# Revit family: Deckel mit Drehriegel_für Kabelrinne und Kabelleiter_NB50
name_source: partatom
category: Generic Models
revit_build: Autodesk Revit 2015 (Build: 20140606_1530(x64)
units: mm (PartAtom-declared; Revit-internal decimal feet)

## types (3) — shared parameters
Height = 13 mm
Length = 3000 mm  [stored 9.84252 ft]
Length 1 = 200 mm  [stored 0.656168 ft]
Length 2 = 1500 mm  [stored 4.92126 ft]
Manufacturer = OBO Bettermann
URL = http://www.obo-bettermann.com
Width = 52 mm
Width 1 = 1 mm  [stored 0.00328084 ft]
Width 2 = 27 mm  [stored 0.0885827 ft]

## per-type parameters (varying)
| type | Article Type | GTIN | Manufacturer Art.No. | Material |
| DRL 050 FS | DRL 050 FS

DRL 050 FS
DRL 050 FS | 4012196057856 | 6052053 | Strip galvanised |
| DRL 050 DD | DRL 050 DD | 4012196038718 | 6052700

6052700
6052700 | Strip galvanised zinc/aluminium |
| DRL 050 FT | DRL 050 FT | 4012196433995 | 6051332 | Hot-dip galvanised |

note: [stored X ft] marks values corroborated as IEEE doubles in the binary element streams (Revit-internal decimal feet)

## geometry (parser evidence)
native form markers: Sweep x3
no freeform markers — native parametric forms only
